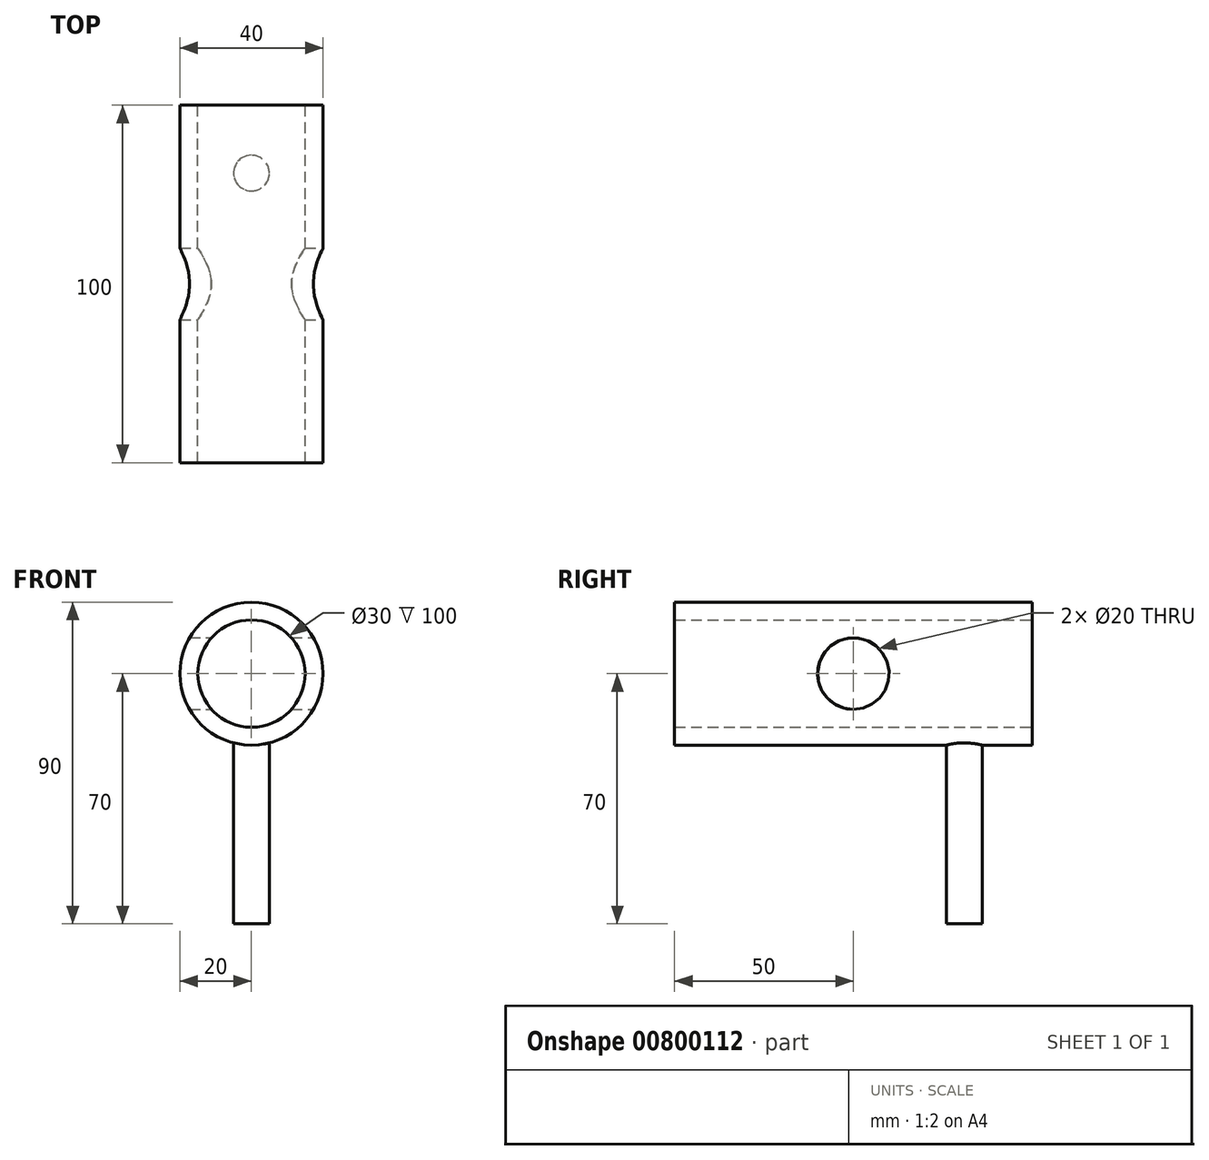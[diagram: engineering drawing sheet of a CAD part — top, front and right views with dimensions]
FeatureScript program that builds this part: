
annotation { "Feature Type Name" : "Feature", "Feature Type Description" : "" }
export const myFeature = defineFeature(function(context is Context, id is Id, definition is map)
    precondition{}
    {
        {
            var Q0;
            Q0=qCreatedBy(makeId("Front.planeOp"),FACE);
            var sketch = newSketch(context, id + "F0", { "sketchPlane" : qUnion([Q0])});
            skCircle(sketch, "E0", {"center": v(0, 0) * mm, "radius": 20 * mm});
            skCircle(sketch, "E1", {"center": v(0, 0) * mm, "radius": 15 * mm});
            skSolve(sketch);
        }
        {
            var Q0;
            Q0=makeQuery(id+"F0.imprint","IMPRINT",FACE,{"disambiguationData":[TD([[makeQuery(id+"F0.imprint","IMPRINT",EDGE,{"derivedFrom":sQuery(id+"F0.wireOp",EDGE,"E0")}),1.0]])]});
            extrude(context, id + "F1", {"entities" : qUnion([Q0]), "endBound" : BoundingType.SYMMETRIC, "depth" : 100 * mm, "offsetDistance" : 25 * mm});
        }
        {
            var Q0;
            Q0=qCreatedBy(makeId("Top.planeOp"),FACE);
            cPlane(context, id + "F2", {"entities" : qUnion([Q0]), "cplaneType" : CPlaneType.OFFSET, "offset" : 20 * mm, "oppositeDirection" : true, "width" : 150 * mm, "height" : 150 * mm});
        }
        {
            var Q0;
            Q0=qCreatedBy(id+"F2.planeOp",FACE);
            var sketch = newSketch(context, id + "F3", { "sketchPlane" : qUnion([Q0])});
            skLineSegment(sketch, "E2", {"start": v(0, 51) * mm, "end": v(0, 31) * mm, "construction": true});
            skCircle(sketch, "E3", {"center": v(0, 31) * mm, "radius": 5 * mm});
            skLineSegment(sketch, "E4", {"start": v(75.78, 0) * mm, "end": v(-82.57, 0) * mm, "construction": true});
            skCircle(sketch, "E5.MirrorC", {"center": v(0, -31) * mm, "radius": 5 * mm});
            skSolve(sketch);
        }
        {
            var Q0;
            Q0=makeQuery(id+"F3.imprint","IMPRINT",FACE,{"disambiguationData":[TD([[makeQuery(id+"F3.imprint","IMPRINT",EDGE,{"derivedFrom":sQuery(id+"F3.wireOp",EDGE,"E3")}),1.0]])]});
            var Q1;
            Q1=makeQuery(id+"F3.imprint","IMPRINT",FACE,{"disambiguationData":[TD([[makeQuery(id+"F3.imprint","IMPRINT",EDGE,{"derivedFrom":sQuery(id+"F3.wireOp",EDGE,"E5.MirrorC")}),-1.0]])]});
            extrude(context, id + "F4", {"entities" : qUnion([Q0, Q1]), "operationType" : NewBodyOperationType.ADD, "oppositeDirection" : true, "depth" : 50 * mm, "offsetDistance" : 25 * mm, "hasSecondDirection" : true, "secondDirectionOppositeDirection" : false, "secondDirectionDepth" : 4 * mm});
        }
        {
            var Q0;
            Q0=qCreatedBy(makeId("Right.planeOp"),FACE);
            cPlane(context, id + "F5", {"entities" : qUnion([Q0]), "cplaneType" : CPlaneType.OFFSET, "offset" : 20 * mm, "width" : 150 * mm, "height" : 150 * mm});
        }
        {
            var Q0;
            Q0=qCreatedBy(id+"F5.planeOp",FACE);
            var sketch = newSketch(context, id + "F6", { "sketchPlane" : qUnion([Q0])});
            skCircle(sketch, "E6", {"center": v(0, 0) * mm, "radius": 10 * mm});
            skSolve(sketch);
        }
        {
            var Q0;
            Q0=makeQuery(id+"F6.imprint","IMPRINT",FACE,{"disambiguationData":[TD([[makeQuery(id+"F6.imprint","IMPRINT",EDGE,{"derivedFrom":sQuery(id+"F6.wireOp",EDGE,"E6")}),1.0]])]});
            extrude(context, id + "F7", {"entities" : qUnion([Q0]), "operationType" : NewBodyOperationType.REMOVE, "oppositeDirection" : true, "depth" : 50 * mm, "offsetDistance" : 25 * mm});
        }
    });
